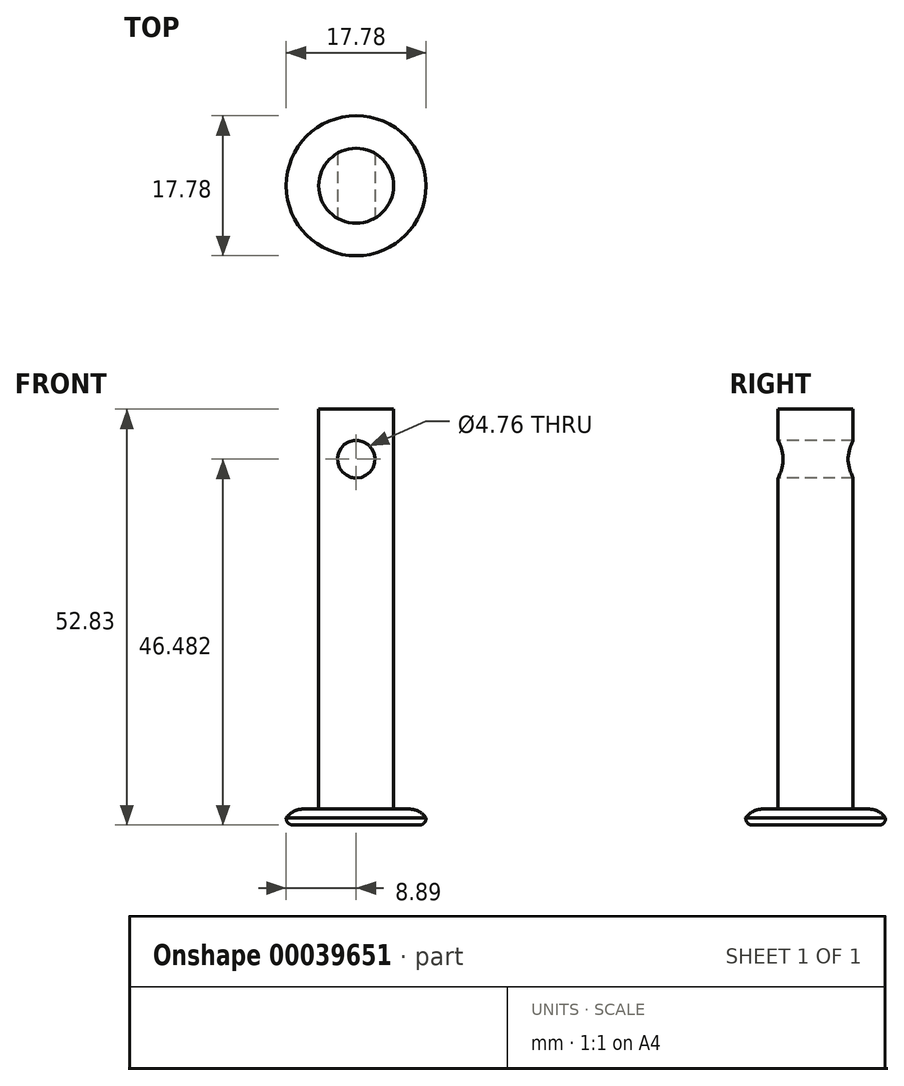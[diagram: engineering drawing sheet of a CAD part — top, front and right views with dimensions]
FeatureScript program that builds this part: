
annotation { "Feature Type Name" : "Feature", "Feature Type Description" : "" }
export const myFeature = defineFeature(function(context is Context, id is Id, definition is map)
    precondition{}
    {
        {
            var Q0;
            Q0=qCreatedBy(makeId("Top.planeOp"),FACE);
            var sketch = newSketch(context, id + "F0", { "sketchPlane" : qUnion([Q0])});
            skCircle(sketch, "E0", {"center": v(0, 0) * mm, "radius": 8.9 * mm});
            skSolve(sketch);
        }
        {
            var Q0;
            Q0=makeQuery(id+"F0.imprint","IMPRINT",FACE,{"disambiguationData":[TD([[makeQuery(id+"F0.imprint","IMPRINT",EDGE,{"derivedFrom":sQuery(id+"F0.wireOp",EDGE,"E0")}),1.0]])]});
            extrude(context, id + "F1", {"entities" : qUnion([Q0]), "depth" : 2.03 * mm});
        }
        {
            var Q0;
            Q0=makeQuery(id+"F1.opExtrude","CAP_FACE",FACE,{"disambiguationData":[OSD([sQuery(id+"F0.wireOp",EDGE,"E0")])],"isStart":false});
            var sketch = newSketch(context, id + "F2", { "sketchPlane" : qUnion([Q0])});
            skCircle(sketch, "E1", {"center": v(0, 0) * mm, "radius": 4.76 * mm});
            skSolve(sketch);
        }
        {
            var Q0;
            Q0=makeQuery(id+"F2.imprint","IMPRINT",FACE,{"disambiguationData":[TD([[makeQuery(id+"F2.imprint","IMPRINT",EDGE,{"derivedFrom":sQuery(id+"F2.wireOp",EDGE,"E1")}),1.0]])]});
            extrude(context, id + "F3", {"entities" : qUnion([Q0]), "operationType" : NewBodyOperationType.ADD, "depth" : 50.8 * mm});
        }
        {
            var Q0;
            Q0=qCreatedBy(makeId("Front.planeOp"),FACE);
            var sketch = newSketch(context, id + "F4", { "sketchPlane" : qUnion([Q0])});
            skLineSegment(sketch, "E2.0", {"start": v(-4.76, 52.83) * mm, "end": v(4.76, 52.83) * mm});
            skLineSegment(sketch, "E3", {"start": v(0, 52.83) * mm, "end": v(0, 46.48) * mm});
            skPoint(sketch, "E3.endSnap0", {"position": v(0, 52.83) * mm});
            skCircle(sketch, "E4", {"center": v(0, 46.48) * mm, "radius": 2.38 * mm});
            skSolve(sketch);
        }
        {
            var Q0;
            Q0=makeQuery(id+"F4.imprint","IMPRINT",FACE,{"disambiguationData":[TD([[makeQuery(id+"F4.imprint","IMPRINT",EDGE,{"derivedFrom":sQuery(id+"F4.wireOp",EDGE,"E4")}),1.0]])]});
            extrude(context, id + "F5", {"entities" : qUnion([Q0]), "operationType" : NewBodyOperationType.REMOVE, "endBound" : BoundingType.SYMMETRIC, "oppositeDirection" : true, "depth" : 9.52 * mm});
        }
        {
            var Q0;
            Q0=makeQuery(id+"F1.opExtrude","CAP_EDGE",EDGE,{"disambiguationData":[OSD([sQuery(id+"F0.wireOp",EDGE,"E0")])],"isStart":true});
            fillet(context, id + "F6", {"entities" : qUnion([Q0]), "radius" : 0.89 * mm, "tangentPropagation" : true, "allowEdgeOverflow" : false});
        }
        {
            var Q0;
            Q0=makeQuery(id+"F1.opExtrude","CAP_EDGE",EDGE,{"disambiguationData":[OSD([sQuery(id+"F0.wireOp",EDGE,"E0")])],"isStart":false});
            fillet(context, id + "F7", {"entities" : qUnion([Q0]), "radius" : 2.54 * mm, "tangentPropagation" : true, "allowEdgeOverflow" : false});
        }
    });
